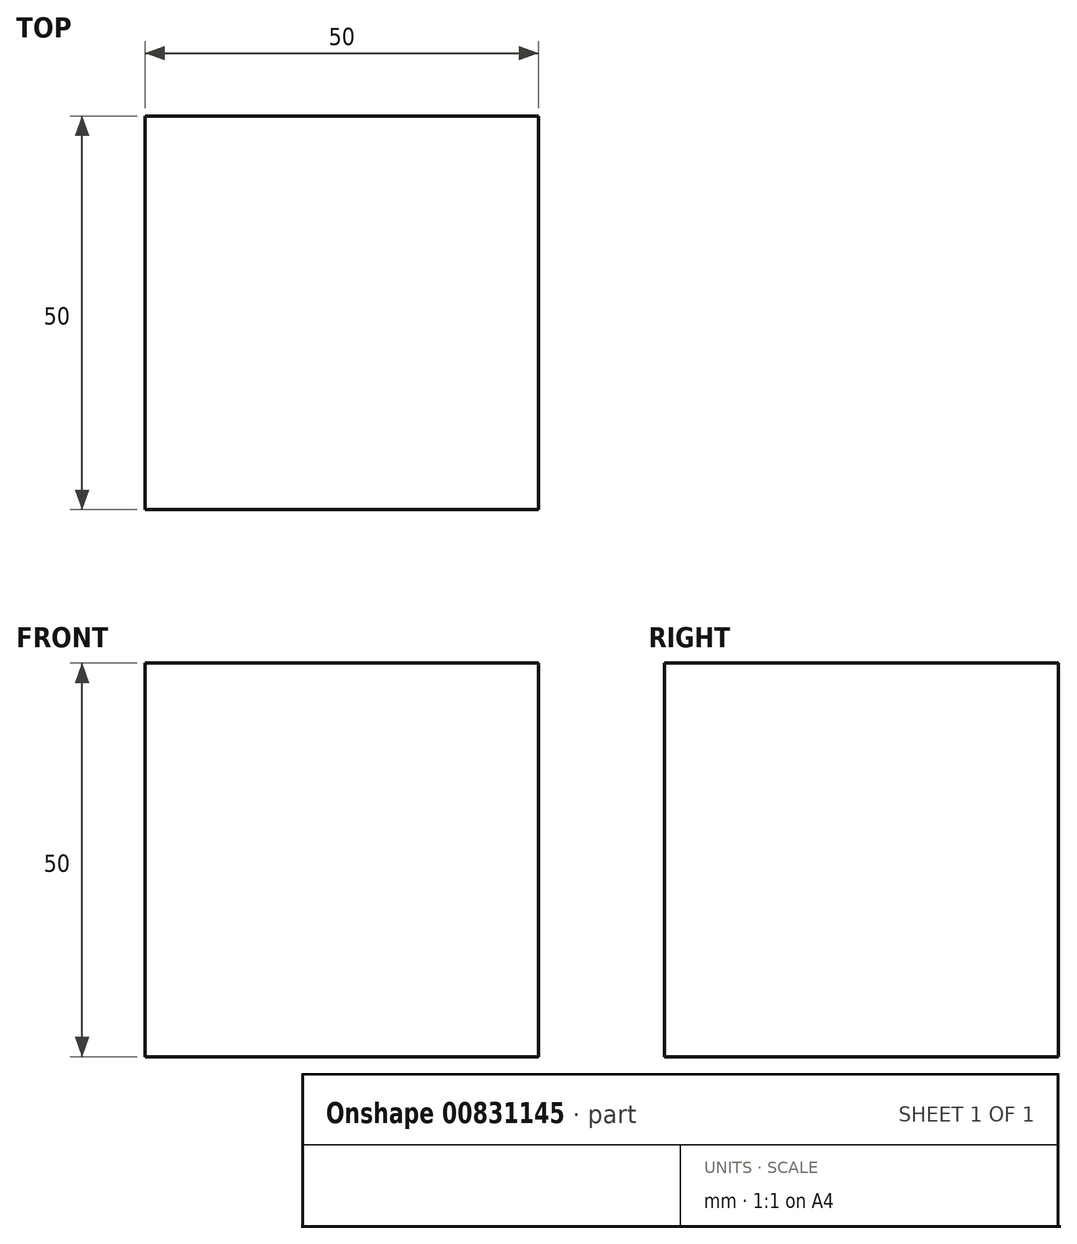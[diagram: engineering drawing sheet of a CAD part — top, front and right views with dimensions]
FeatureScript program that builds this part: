
annotation { "Feature Type Name" : "Feature", "Feature Type Description" : "" }
export const myFeature = defineFeature(function(context is Context, id is Id, definition is map)
    precondition{}
    {
        {
            var Q0;
            Q0=qCreatedBy(makeId("Front.planeOp"),FACE);
            var sketch = newSketch(context, id + "F0", { "sketchPlane" : qUnion([Q0])});
            skLineSegment(sketch, "E0.bottom", {"start": v(-25, 25) * mm, "end": v(25, 25) * mm});
            skLineSegment(sketch, "E0.top", {"start": v(-25, -25) * mm, "end": v(25, -25) * mm});
            skLineSegment(sketch, "E0.left", {"start": v(-25, 25) * mm, "end": v(-25, -25) * mm});
            skLineSegment(sketch, "E0.right", {"start": v(25, 25) * mm, "end": v(25, -25) * mm});
            skPoint(sketch, "E0.middle", {"position": v(0, 0) * mm});
            skSolve(sketch);
        }
        {
            var Q0;
            Q0=makeQuery(id+"F0.imprint","IMPRINT",FACE,{"disambiguationData":[TD([[makeQuery(id+"F0.imprint","IMPRINT",EDGE,{"derivedFrom":sQuery(id+"F0.wireOp",EDGE,"E0.bottom")}),-1.0]])]});
            extrude(context, id + "F1", {"entities" : qUnion([Q0]), "endBound" : BoundingType.SYMMETRIC, "depth" : 50 * mm, "offsetDistance" : 25 * mm});
        }
    });
